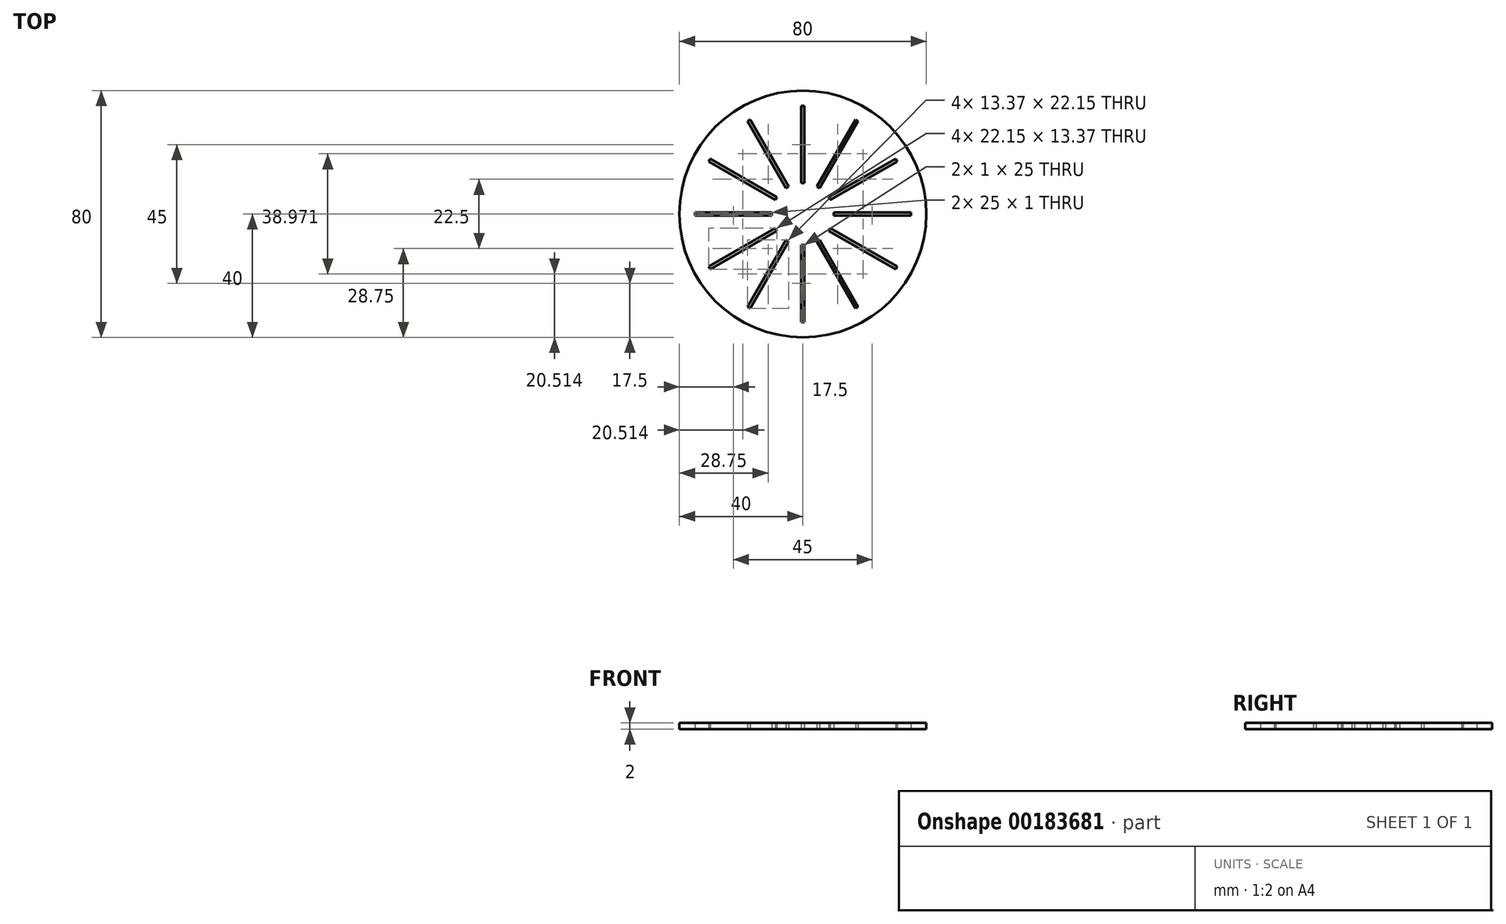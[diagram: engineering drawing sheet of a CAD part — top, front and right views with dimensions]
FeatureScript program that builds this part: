
annotation { "Feature Type Name" : "Feature", "Feature Type Description" : "" }
export const myFeature = defineFeature(function(context is Context, id is Id, definition is map)
    precondition{}
    {
        {
            var Q0;
            Q0=qCreatedBy(makeId("Top.planeOp"),FACE);
            var sketch = newSketch(context, id + "F0", { "sketchPlane" : qUnion([Q0])});
            skCircle(sketch, "E0", {"center": v(0, 0) * mm, "radius": 40 * mm});
            skLineSegment(sketch, "E1.bottom", {"start": v(-0.5, 35) * mm, "end": v(0.5, 35) * mm});
            skLineSegment(sketch, "E1.top", {"start": v(-0.5, 10) * mm, "end": v(0.5, 10) * mm});
            skLineSegment(sketch, "E1.left", {"start": v(-0.5, 35) * mm, "end": v(-0.5, 10) * mm});
            skLineSegment(sketch, "E1.right", {"start": v(0.5, 35) * mm, "end": v(0.5, 10) * mm});
            skLineSegment(sketch, "E2", {"start": v(0, 40) * mm, "end": v(0, 0) * mm, "construction": true});
            skPoint(sketch, "E3", {"position": v(0, 35) * mm});
            skPoint(sketch, "E4", {"position": v(0, 10) * mm});
            skLineSegment(sketch, "E5.1.0", {"start": v(-17.93, 30.06) * mm, "end": v(-5.43, 8.41) * mm});
            skLineSegment(sketch, "E5.1.1", {"start": v(-17.07, 30.56) * mm, "end": v(-4.57, 8.91) * mm});
            skLineSegment(sketch, "E5.1.2", {"start": v(-17.93, 30.06) * mm, "end": v(-17.07, 30.56) * mm});
            skLineSegment(sketch, "E5.1.3", {"start": v(-5.43, 8.41) * mm, "end": v(-4.57, 8.91) * mm});
            skLineSegment(sketch, "E5.2.0", {"start": v(-30.56, 17.07) * mm, "end": v(-8.91, 4.57) * mm});
            skLineSegment(sketch, "E5.2.1", {"start": v(-30.06, 17.93) * mm, "end": v(-8.41, 5.43) * mm});
            skLineSegment(sketch, "E5.2.2", {"start": v(-30.56, 17.07) * mm, "end": v(-30.06, 17.93) * mm});
            skLineSegment(sketch, "E5.2.3", {"start": v(-8.91, 4.57) * mm, "end": v(-8.41, 5.43) * mm});
            skLineSegment(sketch, "E5.3.0", {"start": v(-35, -0.5) * mm, "end": v(-10, -0.5) * mm});
            skLineSegment(sketch, "E5.3.1", {"start": v(-35, 0.5) * mm, "end": v(-10, 0.5) * mm});
            skLineSegment(sketch, "E5.3.2", {"start": v(-35, -0.5) * mm, "end": v(-35, 0.5) * mm});
            skLineSegment(sketch, "E5.3.3", {"start": v(-10, -0.5) * mm, "end": v(-10, 0.5) * mm});
            skLineSegment(sketch, "E5.4.0", {"start": v(-30.06, -17.93) * mm, "end": v(-8.41, -5.43) * mm});
            skLineSegment(sketch, "E5.4.1", {"start": v(-30.56, -17.07) * mm, "end": v(-8.91, -4.57) * mm});
            skLineSegment(sketch, "E5.4.2", {"start": v(-30.06, -17.93) * mm, "end": v(-30.56, -17.07) * mm});
            skLineSegment(sketch, "E5.4.3", {"start": v(-8.41, -5.43) * mm, "end": v(-8.91, -4.57) * mm});
            skLineSegment(sketch, "E5.5.0", {"start": v(-17.07, -30.56) * mm, "end": v(-4.57, -8.91) * mm});
            skLineSegment(sketch, "E5.5.1", {"start": v(-17.93, -30.06) * mm, "end": v(-5.43, -8.41) * mm});
            skLineSegment(sketch, "E5.5.2", {"start": v(-17.07, -30.56) * mm, "end": v(-17.93, -30.06) * mm});
            skLineSegment(sketch, "E5.5.3", {"start": v(-4.57, -8.91) * mm, "end": v(-5.43, -8.41) * mm});
            skLineSegment(sketch, "E5.6.0", {"start": v(0.5, -35) * mm, "end": v(0.5, -10) * mm});
            skLineSegment(sketch, "E5.6.1", {"start": v(-0.5, -35) * mm, "end": v(-0.5, -10) * mm});
            skLineSegment(sketch, "E5.6.2", {"start": v(0.5, -35) * mm, "end": v(-0.5, -35) * mm});
            skLineSegment(sketch, "E5.6.3", {"start": v(0.5, -10) * mm, "end": v(-0.5, -10) * mm});
            skLineSegment(sketch, "E5.7.0", {"start": v(17.93, -30.06) * mm, "end": v(5.43, -8.41) * mm});
            skLineSegment(sketch, "E5.7.1", {"start": v(17.07, -30.56) * mm, "end": v(4.57, -8.91) * mm});
            skLineSegment(sketch, "E5.7.2", {"start": v(17.93, -30.06) * mm, "end": v(17.07, -30.56) * mm});
            skLineSegment(sketch, "E5.7.3", {"start": v(5.43, -8.41) * mm, "end": v(4.57, -8.91) * mm});
            skLineSegment(sketch, "E5.8.0", {"start": v(30.56, -17.07) * mm, "end": v(8.91, -4.57) * mm});
            skLineSegment(sketch, "E5.8.1", {"start": v(30.06, -17.93) * mm, "end": v(8.41, -5.43) * mm});
            skLineSegment(sketch, "E5.8.2", {"start": v(30.56, -17.07) * mm, "end": v(30.06, -17.93) * mm});
            skLineSegment(sketch, "E5.8.3", {"start": v(8.91, -4.57) * mm, "end": v(8.41, -5.43) * mm});
            skLineSegment(sketch, "E5.9.0", {"start": v(35, 0.5) * mm, "end": v(10, 0.5) * mm});
            skLineSegment(sketch, "E5.9.1", {"start": v(35, -0.5) * mm, "end": v(10, -0.5) * mm});
            skLineSegment(sketch, "E5.9.2", {"start": v(35, 0.5) * mm, "end": v(35, -0.5) * mm});
            skLineSegment(sketch, "E5.9.3", {"start": v(10, 0.5) * mm, "end": v(10, -0.5) * mm});
            skLineSegment(sketch, "E5.10.0", {"start": v(30.06, 17.93) * mm, "end": v(8.41, 5.43) * mm});
            skLineSegment(sketch, "E5.10.1", {"start": v(30.56, 17.07) * mm, "end": v(8.91, 4.57) * mm});
            skLineSegment(sketch, "E5.10.2", {"start": v(30.06, 17.93) * mm, "end": v(30.56, 17.07) * mm});
            skLineSegment(sketch, "E5.10.3", {"start": v(8.41, 5.43) * mm, "end": v(8.91, 4.57) * mm});
            skLineSegment(sketch, "E5.11.0", {"start": v(17.07, 30.56) * mm, "end": v(4.57, 8.91) * mm});
            skLineSegment(sketch, "E5.11.1", {"start": v(17.93, 30.06) * mm, "end": v(5.43, 8.41) * mm});
            skLineSegment(sketch, "E5.11.2", {"start": v(17.07, 30.56) * mm, "end": v(17.93, 30.06) * mm});
            skLineSegment(sketch, "E5.11.3", {"start": v(4.57, 8.91) * mm, "end": v(5.43, 8.41) * mm});
            skSolve(sketch);
        }
        {
            var Q0;
            Q0 = qSketchRegion(id + "F0", true);
            extrude(context, id + "F1", {"entities" : qUnion([Q0]), "depth" : 2 * mm});
        }
    });
